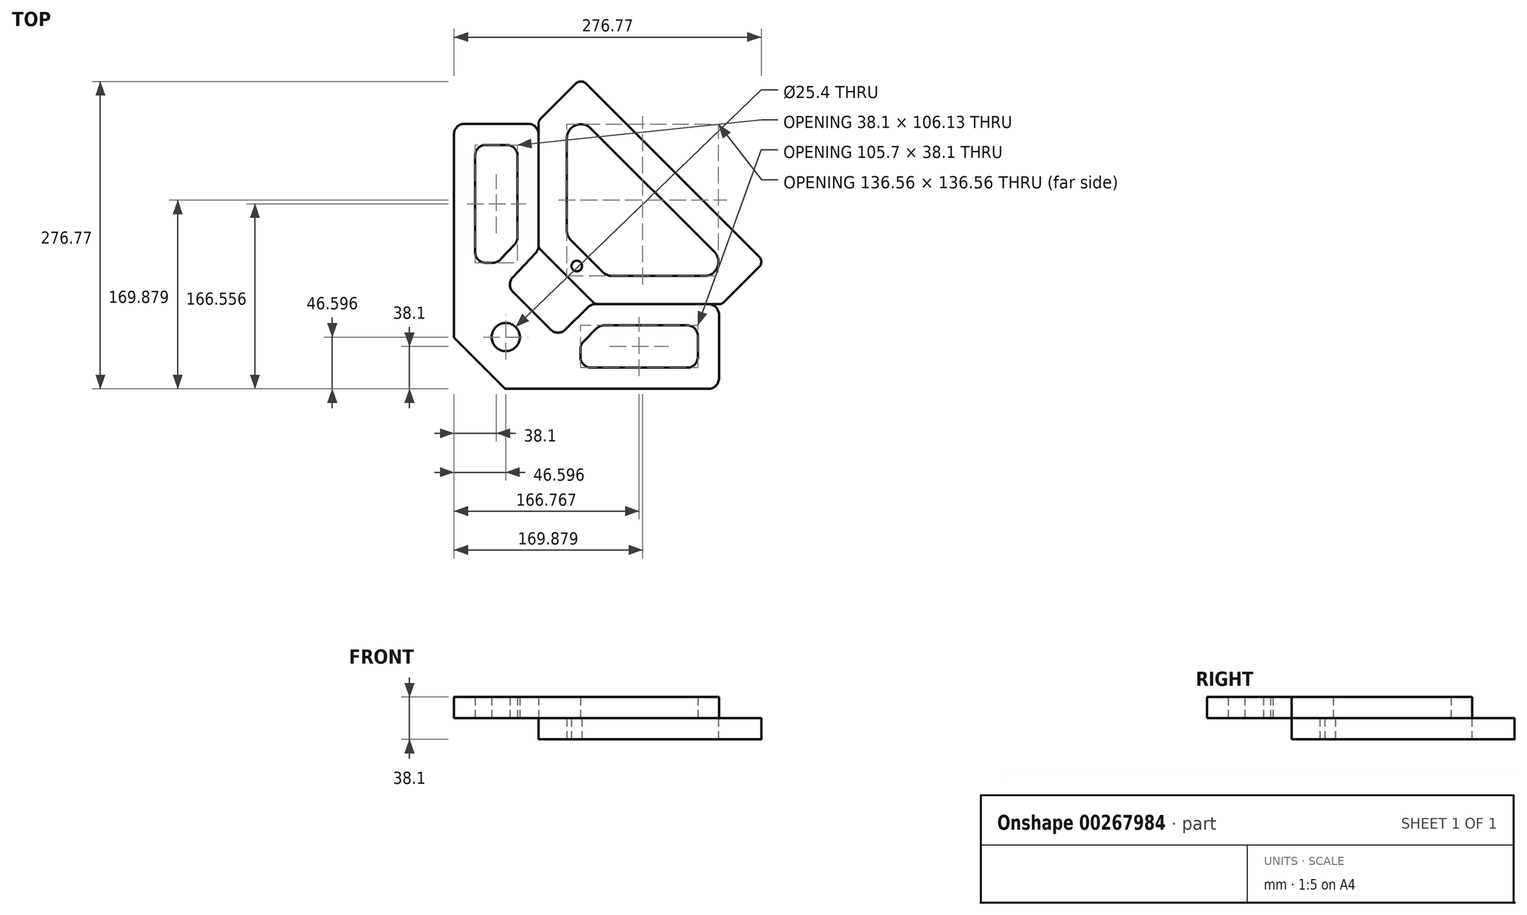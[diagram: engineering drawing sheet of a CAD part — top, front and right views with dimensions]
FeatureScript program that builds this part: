
annotation { "Feature Type Name" : "Feature", "Feature Type Description" : "" }
export const myFeature = defineFeature(function(context is Context, id is Id, definition is map)
    precondition{}
    {
        {
            var Q0;
            Q0=qCreatedBy(makeId("Top.planeOp"),FACE);
            var sketch = newSketch(context, id + "F0", { "sketchPlane" : qUnion([Q0])});
            skLineSegment(sketch, "E0.bottom", {"start": v(-48.17, -101.6) * mm, "end": v(60.87, -101.6) * mm});
            skLineSegment(sketch, "E0.left", {"start": v(-101.6, -48.17) * mm, "end": v(-101.6, 60.87) * mm});
            skPoint(sketch, "E0.middle", {"position": v(0, 0) * mm});
            skLineSegment(sketch, "E1", {"start": v(-50.8, -101.6) * mm, "end": v(-50.8, -50.8) * mm, "construction": true});
            skLineSegment(sketch, "E2", {"start": v(-50.8, -50.8) * mm, "end": v(-101.6, -50.8) * mm, "construction": true});
            skLineSegment(sketch, "E3", {"start": v(-101.6, 63.5) * mm, "end": v(-63.5, 63.5) * mm, "construction": true});
            skLineSegment(sketch, "E4", {"start": v(-63.5, 63.5) * mm, "end": v(-63.5, 101.6) * mm, "construction": true});
            skLineSegment(sketch, "E5", {"start": v(-99.74, 65.36) * mm, "end": v(-68, 97.1) * mm});
            skLineSegment(sketch, "E6", {"start": v(-99.74, -52.66) * mm, "end": v(-52.66, -99.74) * mm});
            skLineSegment(sketch, "E7", {"start": v(-59, 97.1) * mm, "end": v(97.1, -59) * mm});
            skLineSegment(sketch, "E8", {"start": v(65.36, -99.74) * mm, "end": v(97.1, -68) * mm});
            skPoint(sketch, "E9.visualSharp", {"position": v(-63.5, 101.6) * mm});
            skArc(sketch, "E9.filletArc", {"start": v(-59, 97.1) * mm, "mid": v(-63.5, 98.97) * mm, "end": v(-68, 97.1) * mm});
            skPoint(sketch, "E10.visualSharp", {"position": v(-101.6, 63.5) * mm});
            skArc(sketch, "E10.filletArc", {"start": v(-99.74, 65.36) * mm, "mid": v(-101.12, 63.3) * mm, "end": v(-101.6, 60.87) * mm});
            skPoint(sketch, "E11.visualSharp", {"position": v(-101.6, -50.8) * mm});
            skArc(sketch, "E11.filletArc", {"start": v(-101.6, -48.17) * mm, "mid": v(-101.12, -50.6) * mm, "end": v(-99.74, -52.66) * mm});
            skPoint(sketch, "E12.visualSharp", {"position": v(-50.8, -101.6) * mm});
            skArc(sketch, "E12.filletArc", {"start": v(-52.66, -99.74) * mm, "mid": v(-50.6, -101.12) * mm, "end": v(-48.17, -101.6) * mm});
            skPoint(sketch, "E13.visualSharp", {"position": v(63.5, -101.6) * mm});
            skArc(sketch, "E13.filletArc", {"start": v(60.87, -101.6) * mm, "mid": v(63.3, -101.12) * mm, "end": v(65.36, -99.74) * mm});
            skPoint(sketch, "E14.visualSharp", {"position": v(101.6, -63.5) * mm});
            skArc(sketch, "E14.filletArc", {"start": v(97.1, -68) * mm, "mid": v(98.97, -63.5) * mm, "end": v(97.1, -59) * mm});
            skLineSegment(sketch, "E15.0", {"start": v(-72.48, -44) * mm, "end": v(-44, -72.48) * mm});
            skLineSegment(sketch, "E15.1", {"start": v(-72.48, 56.7) * mm, "end": v(-72.48, 56.7) * mm});
            skLineSegment(sketch, "E15.2", {"start": v(-54.52, 56.7) * mm, "end": v(56.7, -54.52) * mm});
            skLineSegment(sketch, "E15.3", {"start": v(-76.2, -35.02) * mm, "end": v(-76.2, 47.72) * mm});
            skLineSegment(sketch, "E15.4", {"start": v(56.7, -72.48) * mm, "end": v(56.7, -72.48) * mm});
            skLineSegment(sketch, "E15.5", {"start": v(-35.02, -76.2) * mm, "end": v(47.72, -76.2) * mm});
            skPoint(sketch, "E16.visualSharp", {"position": v(-63.5, 65.68) * mm});
            skArc(sketch, "E16.filletArc", {"start": v(-54.52, 56.7) * mm, "mid": v(-63.5, 60.42) * mm, "end": v(-72.48, 56.7) * mm});
            skPoint(sketch, "E17.visualSharp", {"position": v(-76.2, 52.98) * mm});
            skArc(sketch, "E17.filletArc", {"start": v(-72.48, 56.7) * mm, "mid": v(-75.23, 52.58) * mm, "end": v(-76.2, 47.72) * mm});
            skPoint(sketch, "E18.visualSharp", {"position": v(-76.2, -40.28) * mm});
            skArc(sketch, "E18.filletArc", {"start": v(-76.2, -35.02) * mm, "mid": v(-75.23, -39.88) * mm, "end": v(-72.48, -44) * mm});
            skPoint(sketch, "E19.visualSharp", {"position": v(-40.28, -76.2) * mm});
            skArc(sketch, "E19.filletArc", {"start": v(-44, -72.48) * mm, "mid": v(-39.88, -75.23) * mm, "end": v(-35.02, -76.2) * mm});
            skPoint(sketch, "E20.visualSharp", {"position": v(52.98, -76.2) * mm});
            skArc(sketch, "E20.filletArc", {"start": v(47.72, -76.2) * mm, "mid": v(52.58, -75.23) * mm, "end": v(56.7, -72.48) * mm});
            skPoint(sketch, "E21.visualSharp", {"position": v(65.68, -63.5) * mm});
            skArc(sketch, "E21.filletArc", {"start": v(56.7, -72.48) * mm, "mid": v(60.42, -63.5) * mm, "end": v(56.7, -54.52) * mm});
            skLineSegment(sketch, "E22", {"start": v(-58.24, -58.24) * mm, "end": v(-76.2, -76.2) * mm, "construction": true});
            skCircle(sketch, "E23", {"center": v(-67.22, -67.22) * mm, "radius": 4.76 * mm});
            skSolve(sketch);
        }
        {
            var Q0;
            Q0=makeQuery(id+"F0.imprint","IMPRINT",FACE,{"disambiguationData":[TD([[makeQuery(id+"F0.imprint","IMPRINT",EDGE,{"derivedFrom":sQuery(id+"F0.wireOp",EDGE,"E0.bottom")}),1.0]])]});
            extrude(context, id + "F1", {"entities" : qUnion([Q0]), "depth" : 19.05 * mm});
        }
        {
            var Q0;
            Q0=makeQuery(id+"F1.opExtrude","CAP_FACE",FACE,{"disambiguationData":[OSD([sQuery(id+"F0.wireOp",EDGE,"E0.bottom"),sQuery(id+"F0.wireOp",EDGE,"E0.left"),sQuery(id+"F0.wireOp",EDGE,"E5"),sQuery(id+"F0.wireOp",EDGE,"E6"),sQuery(id+"F0.wireOp",EDGE,"E7"),sQuery(id+"F0.wireOp",EDGE,"E8"),sQuery(id+"F0.wireOp",EDGE,"E9.filletArc"),sQuery(id+"F0.wireOp",EDGE,"E10.filletArc"),sQuery(id+"F0.wireOp",EDGE,"E11.filletArc"),sQuery(id+"F0.wireOp",EDGE,"E12.filletArc"),sQuery(id+"F0.wireOp",EDGE,"E13.filletArc"),sQuery(id+"F0.wireOp",EDGE,"E14.filletArc"),sQuery(id+"F0.wireOp",EDGE,"E15.0"),sQuery(id+"F0.wireOp",EDGE,"E15.2"),sQuery(id+"F0.wireOp",EDGE,"E15.3"),sQuery(id+"F0.wireOp",EDGE,"E15.5"),sQuery(id+"F0.wireOp",EDGE,"E16.filletArc"),sQuery(id+"F0.wireOp",EDGE,"E17.filletArc"),sQuery(id+"F0.wireOp",EDGE,"E18.filletArc"),sQuery(id+"F0.wireOp",EDGE,"E19.filletArc"),sQuery(id+"F0.wireOp",EDGE,"E20.filletArc"),sQuery(id+"F0.wireOp",EDGE,"E21.filletArc")])],"isStart":false});
            var sketch = newSketch(context, id + "F2", { "sketchPlane" : qUnion([Q0])});
            skLineSegment(sketch, "E24", {"start": v(-101.6, 51.34) * mm, "end": v(-101.6, -48.88) * mm});
            skLineSegment(sketch, "E25", {"start": v(51.34, -101.6) * mm, "end": v(-50.57, -101.6) * mm});
            skLineSegment(sketch, "E26.0", {"start": v(51.34, -177.8) * mm, "end": v(-131.75, -177.8) * mm});
            skLineSegment(sketch, "E26.1", {"start": v(-177.8, 51.34) * mm, "end": v(-177.8, -131.75) * mm});
            skLineSegment(sketch, "E27.0", {"start": v(-178.32, -131.24) * mm, "end": v(-131.24, -178.32) * mm});
            skLineSegment(sketch, "E28.0", {"start": v(-124.64, -90.62) * mm, "end": v(-90.83, -124.44) * mm});
            skLineSegment(sketch, "E29", {"start": v(-124.84, -77.36) * mm, "end": v(-104.19, -55.41) * mm});
            skLineSegment(sketch, "E30", {"start": v(-77.36, -124.44) * mm, "end": v(-57.3, -104.39) * mm});
            skLineSegment(sketch, "E31", {"start": v(-168.27, 60.87) * mm, "end": v(-111.12, 60.87) * mm});
            skLineSegment(sketch, "E32", {"start": v(60.87, -111.13) * mm, "end": v(60.87, -168.28) * mm});
            skPoint(sketch, "E33.visualSharp", {"position": v(-177.8, 60.87) * mm});
            skArc(sketch, "E33.filletArc", {"start": v(-168.27, 60.87) * mm, "mid": v(-175.01, 58.08) * mm, "end": v(-177.8, 51.34) * mm});
            skPoint(sketch, "E34.visualSharp", {"position": v(-101.6, 60.87) * mm});
            skArc(sketch, "E34.filletArc", {"start": v(-101.6, 51.34) * mm, "mid": v(-104.39, 58.08) * mm, "end": v(-111.12, 60.87) * mm});
            skPoint(sketch, "E35.visualSharp", {"position": v(60.87, -101.6) * mm});
            skArc(sketch, "E35.filletArc", {"start": v(60.87, -111.13) * mm, "mid": v(58.08, -104.39) * mm, "end": v(51.34, -101.6) * mm});
            skPoint(sketch, "E36.visualSharp", {"position": v(60.87, -177.8) * mm});
            skArc(sketch, "E36.filletArc", {"start": v(51.34, -177.8) * mm, "mid": v(58.08, -175.01) * mm, "end": v(60.87, -168.28) * mm});
            skPoint(sketch, "E37.visualSharp", {"position": v(-84.1, -131.17) * mm});
            skArc(sketch, "E37.filletArc", {"start": v(-90.83, -124.44) * mm, "mid": v(-84.1, -127.23) * mm, "end": v(-77.36, -124.44) * mm});
            skPoint(sketch, "E38.visualSharp", {"position": v(-131.17, -84.1) * mm});
            skArc(sketch, "E38.filletArc", {"start": v(-124.84, -77.36) * mm, "mid": v(-127.43, -84.03) * mm, "end": v(-124.64, -90.62) * mm});
            skPoint(sketch, "E39.visualSharp", {"position": v(-54.52, -101.6) * mm});
            skArc(sketch, "E39.filletArc", {"start": v(-50.57, -101.6) * mm, "mid": v(-54.22, -102.33) * mm, "end": v(-57.3, -104.39) * mm});
            skPoint(sketch, "E40.visualSharp", {"position": v(-101.6, -52.66) * mm});
            skArc(sketch, "E40.filletArc", {"start": v(-104.19, -55.41) * mm, "mid": v(-102.27, -52.4) * mm, "end": v(-101.6, -48.88) * mm});
            skLineSegment(sketch, "E41.0", {"start": v(-158.75, 32.3) * mm, "end": v(-158.75, -54.78) * mm});
            skLineSegment(sketch, "E41.1", {"start": v(-61.1, -135.12) * mm, "end": v(-49.42, -123.44) * mm});
            skLineSegment(sketch, "E41.2", {"start": v(32.3, -120.65) * mm, "end": v(-42.68, -120.65) * mm});
            skLineSegment(sketch, "E41.3", {"start": v(41.82, -130.18) * mm, "end": v(41.82, -149.22) * mm});
            skLineSegment(sketch, "E41.4", {"start": v(32.3, -158.75) * mm, "end": v(-54.36, -158.75) * mm});
            skLineSegment(sketch, "E41.8", {"start": v(-135.9, -61.3) * mm, "end": v(-123.24, -47.86) * mm});
            skLineSegment(sketch, "E41.9", {"start": v(-120.65, 32.3) * mm, "end": v(-120.65, -41.33) * mm});
            skLineSegment(sketch, "E41.10", {"start": v(-149.22, 41.82) * mm, "end": v(-130.18, 41.82) * mm});
            skLineSegment(sketch, "E42", {"start": v(-142.83, -64.3) * mm, "end": v(-149.22, -64.3) * mm});
            skLineSegment(sketch, "E43", {"start": v(-63.89, -141.85) * mm, "end": v(-63.89, -149.22) * mm});
            skPoint(sketch, "E44.visualSharp", {"position": v(-158.75, 41.82) * mm});
            skArc(sketch, "E44.filletArc", {"start": v(-149.22, 41.82) * mm, "mid": v(-155.96, 39.03) * mm, "end": v(-158.75, 32.3) * mm});
            skPoint(sketch, "E45.visualSharp", {"position": v(-120.65, 41.82) * mm});
            skArc(sketch, "E45.filletArc", {"start": v(-120.65, 32.3) * mm, "mid": v(-123.44, 39.03) * mm, "end": v(-130.18, 41.82) * mm});
            skPoint(sketch, "E46.visualSharp", {"position": v(-120.65, -45.1) * mm});
            skArc(sketch, "E46.filletArc", {"start": v(-123.24, -47.86) * mm, "mid": v(-121.32, -44.84) * mm, "end": v(-120.65, -41.33) * mm});
            skPoint(sketch, "E47.visualSharp", {"position": v(-138.71, -64.3) * mm});
            skArc(sketch, "E47.filletArc", {"start": v(-142.83, -64.3) * mm, "mid": v(-139.05, -63.53) * mm, "end": v(-135.9, -61.3) * mm});
            skPoint(sketch, "E48.visualSharp", {"position": v(-158.75, -64.3) * mm});
            skArc(sketch, "E48.filletArc", {"start": v(-158.75, -54.78) * mm, "mid": v(-155.96, -61.52) * mm, "end": v(-149.22, -64.3) * mm});
            skPoint(sketch, "E49.visualSharp", {"position": v(-63.89, -158.75) * mm});
            skArc(sketch, "E49.filletArc", {"start": v(-63.89, -149.22) * mm, "mid": v(-61.1, -155.96) * mm, "end": v(-54.36, -158.75) * mm});
            skPoint(sketch, "E50.visualSharp", {"position": v(-63.89, -137.9) * mm});
            skArc(sketch, "E50.filletArc", {"start": v(-61.1, -135.12) * mm, "mid": v(-63.16, -138.2) * mm, "end": v(-63.89, -141.85) * mm});
            skPoint(sketch, "E51.visualSharp", {"position": v(-46.63, -120.65) * mm});
            skArc(sketch, "E51.filletArc", {"start": v(-42.68, -120.65) * mm, "mid": v(-46.33, -121.38) * mm, "end": v(-49.42, -123.44) * mm});
            skPoint(sketch, "E52.visualSharp", {"position": v(41.82, -120.65) * mm});
            skArc(sketch, "E52.filletArc", {"start": v(41.82, -130.18) * mm, "mid": v(39.03, -123.44) * mm, "end": v(32.3, -120.65) * mm});
            skPoint(sketch, "E53.visualSharp", {"position": v(41.82, -158.75) * mm});
            skArc(sketch, "E53.filletArc", {"start": v(32.3, -158.75) * mm, "mid": v(39.03, -155.96) * mm, "end": v(41.82, -149.22) * mm});
            skLineSegment(sketch, "E54", {"start": v(-154.78, -154.78) * mm, "end": v(-107.63, -107.63) * mm, "construction": true});
            skCircle(sketch, "E55", {"center": v(-131.2, -131.2) * mm, "radius": 12.7 * mm});
            skSolve(sketch);
        }
        {
            var Q0;
            {var subQ1=sQuery(id+"F2.wireOp",EDGE,"E26.0");Q0=makeQuery(id+"F2.imprint","IMPRINT",FACE,{"disambiguationData":[TD([[makeQuery(id+"F2.imprint","IMPRINT",EDGE,{"derivedFrom":subQ1}),-1.0]])]});}
            extrude(context, id + "F3", {"entities" : qUnion([Q0]), "depth" : 19.05 * mm});
        }
        {
            var Q0;
            Q0=makeQuery(id+"F3.opExtrude","SWEPT_EDGE",EDGE,{"disambiguationData":[OSD([sQuery(id+"F2.wireOp",EDGE,"E26.0"),sQuery(id+"F2.wireOp",EDGE,"E27.0")])]});
            var Q1;
            Q1=makeQuery(id+"F3.opExtrude","SWEPT_EDGE",EDGE,{"disambiguationData":[OSD([sQuery(id+"F2.wireOp",EDGE,"E26.1"),sQuery(id+"F2.wireOp",EDGE,"E27.0")])]});
            fillet(context, id + "F4", {"entities" : qUnion([Q0, Q1]), "radius" : 3.17 * mm, "tangentPropagation" : true, "allowEdgeOverflow" : false});
        }
    });
